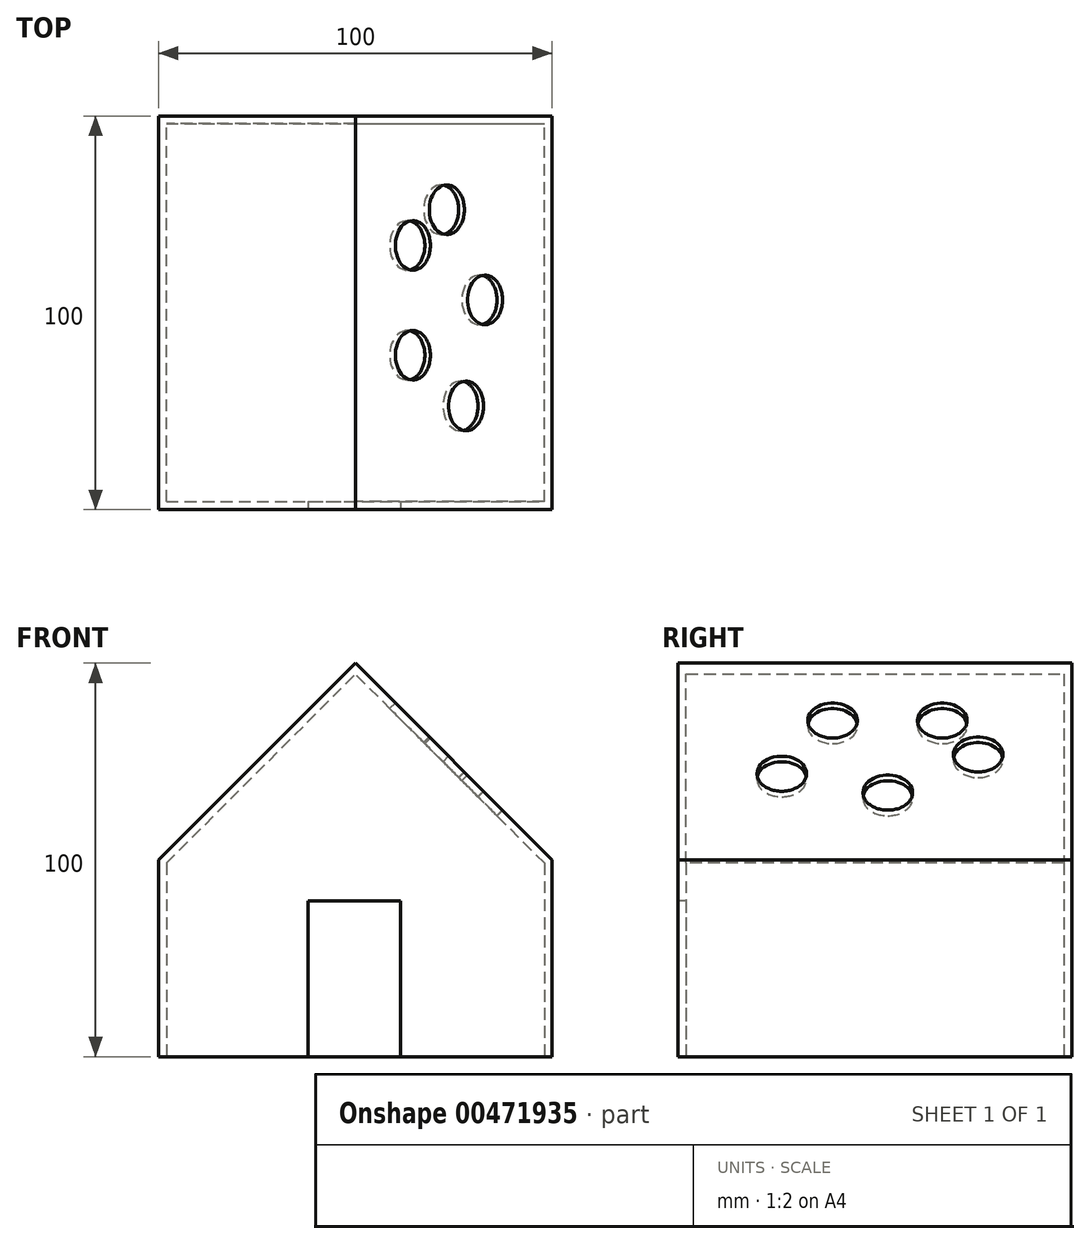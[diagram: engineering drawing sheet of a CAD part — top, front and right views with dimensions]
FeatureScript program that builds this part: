
annotation { "Feature Type Name" : "Feature", "Feature Type Description" : "" }
export const myFeature = defineFeature(function(context is Context, id is Id, definition is map)
    precondition{}
    {
        {
            var Q0;
            Q0=qCreatedBy(makeId("Top.planeOp"),FACE);
            var sketch = newSketch(context, id + "F0", { "sketchPlane" : qUnion([Q0])});
            skLineSegment(sketch, "E0.bottom", {"start": v(-50, -50) * mm, "end": v(50, -50) * mm});
            skLineSegment(sketch, "E0.top", {"start": v(-50, 50) * mm, "end": v(50, 50) * mm});
            skLineSegment(sketch, "E0.left", {"start": v(-50, -50) * mm, "end": v(-50, 50) * mm});
            skLineSegment(sketch, "E0.right", {"start": v(50, -50) * mm, "end": v(50, 50) * mm});
            skPoint(sketch, "E0.middle", {"position": v(0, 0) * mm});
            skSolve(sketch);
        }
        {
            var Q0;
            Q0=makeQuery(id+"F0.imprint","IMPRINT",FACE,{"disambiguationData":[TD([[makeQuery(id+"F0.imprint","IMPRINT",EDGE,{"derivedFrom":sQuery(id+"F0.wireOp",EDGE,"E0.bottom")}),1.0]])]});
            extrude(context, id + "F1", {"entities" : qUnion([Q0]), "depth" : 100 * mm});
        }
        {
            var Q0;
            Q0=makeQuery(id+"F1.opExtrude","CAP_EDGE",EDGE,{"disambiguationData":[OSD([sQuery(id+"F0.wireOp",EDGE,"E0.left")])],"isStart":false});
            var Q1;
            Q1=makeQuery(id+"F1.opExtrude","CAP_EDGE",EDGE,{"disambiguationData":[OSD([sQuery(id+"F0.wireOp",EDGE,"E0.right")])],"isStart":false});
            chamfer(context, id + "F2", {"entities" : qUnion([Q0, Q1]), "chamferType" : ChamferType.OFFSET_ANGLE, "width" : 50 * mm, "oppositeDirection" : false, "angle" : 45 * degree, "tangentPropagation" : true});
        }
        {
            var Q0;
            Q0=makeQuery(id+"F1.opExtrude","CAP_FACE",FACE,{"disambiguationData":[OSD([sQuery(id+"F0.wireOp",EDGE,"E0.bottom"),sQuery(id+"F0.wireOp",EDGE,"E0.top"),sQuery(id+"F0.wireOp",EDGE,"E0.left"),sQuery(id+"F0.wireOp",EDGE,"E0.right")])],"isStart":true});
            shell(context, id + "F3", {"entities" : qUnion([Q0]), "thickness" : 2 * mm});
        }
        {
            var Q0;
            Q0=makeQuery(id+"F1.opExtrude","SWEPT_FACE",FACE,{"disambiguationData":[OSD([sQuery(id+"F0.wireOp",EDGE,"E0.bottom")])]});
            var sketch = newSketch(context, id + "F4", { "sketchPlane" : qUnion([Q0])});
            skLineSegment(sketch, "E1.bottom", {"start": v(-12.1, 39.54) * mm, "end": v(11.42, 39.54) * mm});
            skLineSegment(sketch, "E1.top", {"start": v(-12.1, 0) * mm, "end": v(11.42, 0) * mm});
            skLineSegment(sketch, "E1.left", {"start": v(-12.1, 39.54) * mm, "end": v(-12.1, 0) * mm});
            skLineSegment(sketch, "E1.right", {"start": v(11.42, 39.54) * mm, "end": v(11.42, 0) * mm});
            skSolve(sketch);
        }
        {
            var Q0;
            Q0 = qSketchRegion(id + "F4", true);
            extrude(context, id + "F5", {"entities" : qUnion([Q0]), "operationType" : NewBodyOperationType.REMOVE, "endBound" : BoundingType.UP_TO_NEXT, "oppositeDirection" : true, "depth" : 25 * mm});
        }
        {
            var Q0;
            Q0=makeQuery(id+"F2.opChamfer","BLEND_FACE",FACE,{"disambiguationData":[OSD([sQuery(id+"F0.wireOp",EDGE,"E0.right")])]});
            var sketch = newSketch(context, id + "F6", { "sketchPlane" : qUnion([Q0])});
            skPoint(sketch, "E2", {"position": v(17.1, 50.07) * mm});
            skPoint(sketch, "E3", {"position": v(-10.78, 50.07) * mm});
            skPoint(sketch, "E4", {"position": v(26.2, 37.88) * mm});
            skPoint(sketch, "E5", {"position": v(-23.68, 30.96) * mm});
            skPoint(sketch, "E6", {"position": v(3.27, 24.16) * mm});
            skSolve(sketch);
        }
        {
            var Q0;
            Q0=sQuery(id+"F6.wireOp",VERTEX,"E2");
            var Q1;
            Q1=sQuery(id+"F6.wireOp",VERTEX,"E3");
            var Q2;
            Q2=sQuery(id+"F6.wireOp",VERTEX,"E5");
            var Q3;
            Q3=sQuery(id+"F6.wireOp",VERTEX,"E6");
            var Q4;
            Q4=sQuery(id+"F6.wireOp",VERTEX,"E4");
            var Q5;
            Q5=makeQuery(id+"F1.opExtrude","SWEPT_BODY",BODY,{"disambiguationData":[OSD([sQuery(id+"F0.wireOp",EDGE,"E0.bottom"),sQuery(id+"F0.wireOp",EDGE,"E0.top"),sQuery(id+"F0.wireOp",EDGE,"E0.left"),sQuery(id+"F0.wireOp",EDGE,"E0.right")])]});
            hole(context, id + "F7", {"style" : HoleStyle.SIMPLE, "endStyle" : HoleEndStyle.BLIND, "standardTappedOrClearance" : lookupTablePath({ "standard" : "ISO", "fit" : "Close", "size" : "M12", "type" : "Clearance" }), "standardBlindInLast" : lookupTablePath({ "fit" : "Close", "standard" : "ISO", "size" : "M12", "type" : "Clearance" }), "holeDiameter" : 12.6 * mm, "holeDepth" : 17.25 * mm, "isTappedThrough" : true, "tappedDepth" : 12 * mm, "tapClearance" : 3, "locations" : qUnion([Q0, Q1, Q2, Q3, Q4]), "scope" : qUnion([Q5])});
        }
    });
